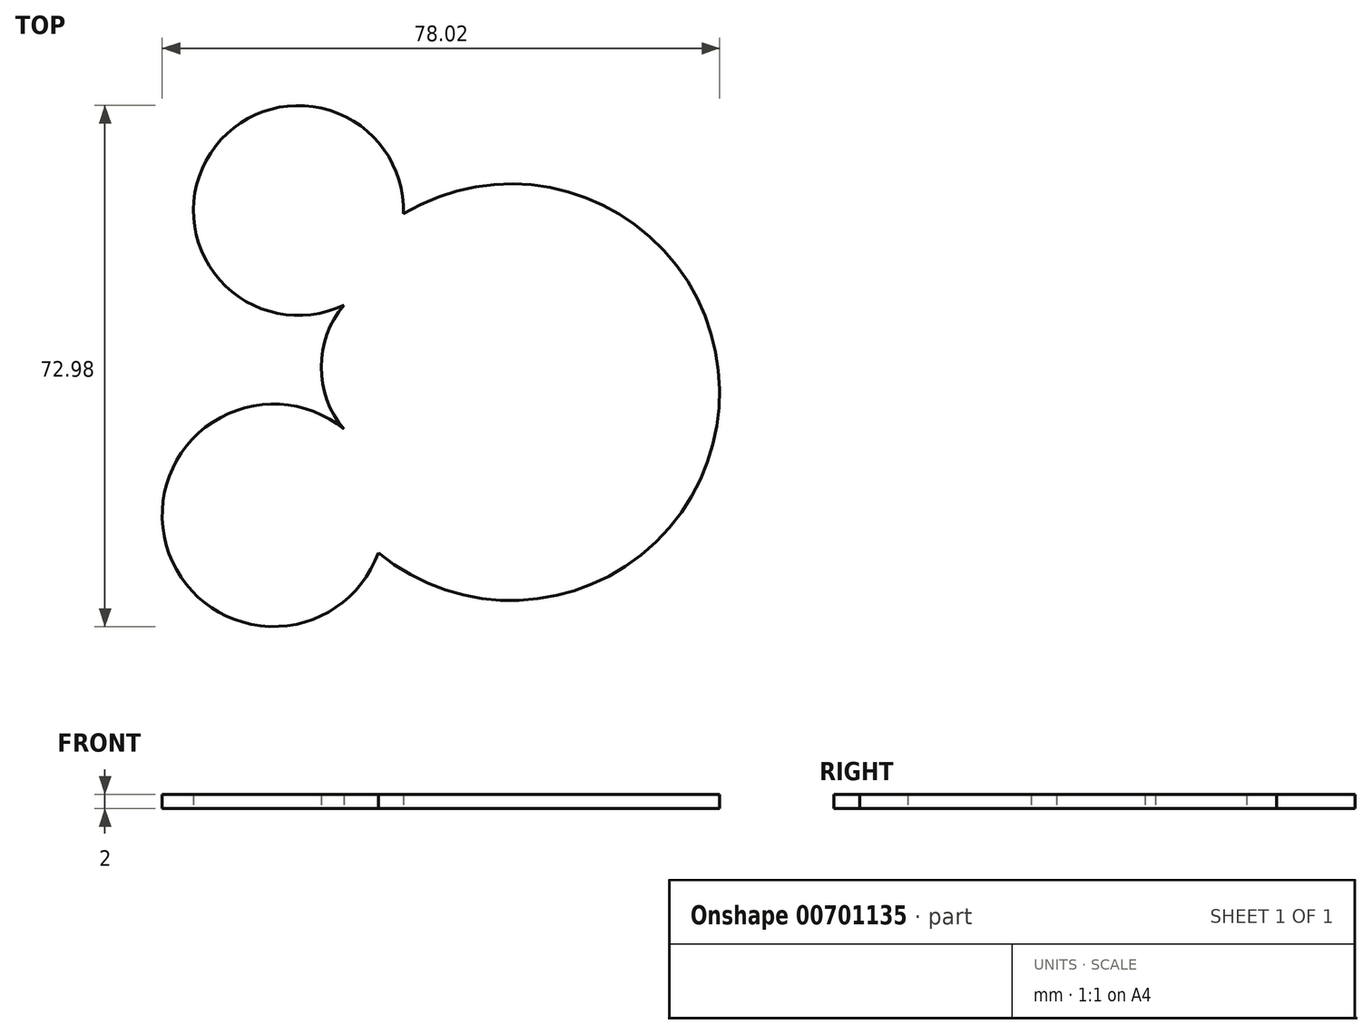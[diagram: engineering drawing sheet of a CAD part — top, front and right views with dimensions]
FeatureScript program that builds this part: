
annotation { "Feature Type Name" : "Feature", "Feature Type Description" : "" }
export const myFeature = defineFeature(function(context is Context, id is Id, definition is map)
    precondition{}
    {
        {
            var Q0;
            Q0=qCreatedBy(makeId("Top.planeOp"),FACE);
            var sketch = newSketch(context, id + "F0", { "sketchPlane" : qUnion([Q0])});
            skArc(sketch, "E0", {"start": v(-60.41, -7.7) * mm, "mid": v(-12.73, 12.65) * mm, "end": v(-56.9, 39.78) * mm});
            skArc(sketch, "E1", {"start": v(-56.9, 39.78) * mm, "mid": v(-83.91, 48.27) * mm, "end": v(-65.22, 27) * mm});
            skArc(sketch, "E2", {"start": v(-65.22, 27) * mm, "mid": v(-68.4, 18.3) * mm, "end": v(-65.22, 9.61) * mm});
            skArc(sketch, "E3", {"start": v(-65.22, 9.61) * mm, "mid": v(-90.1, -6.61) * mm, "end": v(-60.41, -7.7) * mm});
            skLineSegment(sketch, "E4", {"start": v(-60.41, -7.7) * mm, "end": v(-60.41, -7.7) * mm});
            skSolve(sketch);
        }
        {
            var Q0;
            Q0=makeQuery(id+"F0.imprint","IMPRINT",FACE,{"disambiguationData":[TD([[makeQuery(id+"F0.imprint","IMPRINT",EDGE,{"derivedFrom":sQuery(id+"F0.wireOp",EDGE,"E0")}),1.0]])]});
            extrude(context, id + "F1", {"entities" : qUnion([Q0]), "depth" : 2 * mm, "offsetDistance" : 25.4 * mm});
        }
    });
